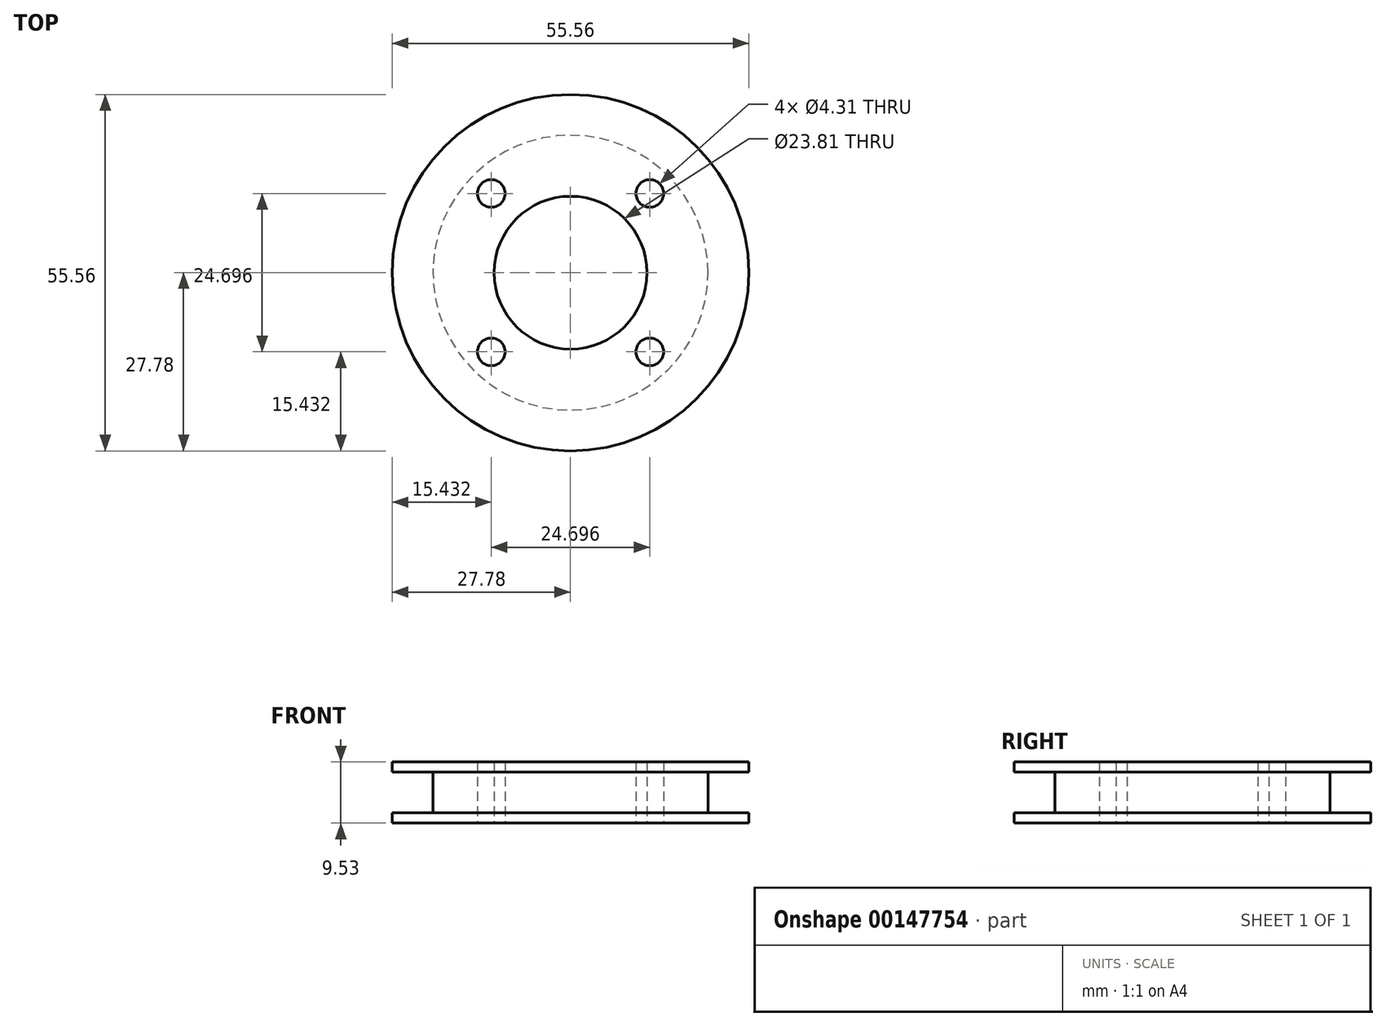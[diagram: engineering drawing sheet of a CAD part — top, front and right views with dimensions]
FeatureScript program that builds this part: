
annotation { "Feature Type Name" : "Feature", "Feature Type Description" : "" }
export const myFeature = defineFeature(function(context is Context, id is Id, definition is map)
    precondition{}
    {
        {
            var Q0;
            Q0=qCreatedBy(makeId("Top.planeOp"),FACE);
            var sketch = newSketch(context, id + "F0", { "sketchPlane" : qUnion([Q0])});
            skCircle(sketch, "E0", {"center": v(0, 0) * mm, "radius": 27.78 * mm});
            skCircle(sketch, "E1", {"center": v(0, 0) * mm, "radius": 11.9 * mm});
            skLineSegment(sketch, "E2.bottom", {"start": v(-12.35, 12.35) * mm, "end": v(12.35, 12.35) * mm, "construction": true});
            skLineSegment(sketch, "E2.top", {"start": v(-12.35, -12.35) * mm, "end": v(12.35, -12.35) * mm, "construction": true});
            skLineSegment(sketch, "E2.left", {"start": v(-12.35, 12.35) * mm, "end": v(-12.35, -12.35) * mm, "construction": true});
            skLineSegment(sketch, "E2.right", {"start": v(12.35, 12.35) * mm, "end": v(12.35, -12.35) * mm, "construction": true});
            skCircle(sketch, "E3", {"center": v(-12.35, 12.35) * mm, "radius": 5.56 * mm, "construction": true});
            skCircle(sketch, "E4", {"center": v(12.35, 12.35) * mm, "radius": 2.15 * mm});
            skCircle(sketch, "E5", {"center": v(-12.35, 12.35) * mm, "radius": 2.15 * mm});
            skCircle(sketch, "E6", {"center": v(-12.35, -12.35) * mm, "radius": 2.15 * mm});
            skCircle(sketch, "E7", {"center": v(12.35, -12.35) * mm, "radius": 2.15 * mm});
            skSolve(sketch);
        }
        {
            var Q0;
            Q0=qSketchRegion(id+"F0",true);
            extrude(context, id + "F1", {"entities" : qUnion([Q0]), "depth" : 9.52 * mm});
        }
        {
            var Q0;
            Q0=qCreatedBy(makeId("Front.planeOp"),FACE);
            var sketch = newSketch(context, id + "F2", { "sketchPlane" : qUnion([Q0])});
            skLineSegment(sketch, "E8.bottom", {"start": v(-42.86, 7.94) * mm, "end": v(-21.43, 7.94) * mm});
            skLineSegment(sketch, "E8.top", {"start": v(-42.86, 1.59) * mm, "end": v(-21.43, 1.59) * mm});
            skLineSegment(sketch, "E8.left", {"start": v(-42.86, 7.94) * mm, "end": v(-42.86, 1.59) * mm});
            skLineSegment(sketch, "E8.right", {"start": v(-21.43, 7.94) * mm, "end": v(-21.43, 1.59) * mm});
            skLineSegment(sketch, "E9", {"start": v(-21.43, 7.94) * mm, "end": v(-21.43, 9.53) * mm, "construction": true});
            skLineSegment(sketch, "E10", {"start": v(-21.43, 9.53) * mm, "end": v(0, 9.53) * mm, "construction": true});
            skLineSegment(sketch, "E11", {"start": v(-21.43, 1.59) * mm, "end": v(-21.43, 0) * mm, "construction": true});
            skLineSegment(sketch, "E12", {"start": v(-21.43, 0) * mm, "end": v(0, 0) * mm, "construction": true});
            skSolve(sketch);
        }
        {
            var Q0;
            Q0=qSketchRegion(id+"F2",true);
            var Q1;
            Q1=makeQuery(id+"F1.opExtrude","SWEPT_FACE",FACE,{"disambiguationData":[OSD([sQuery(id+"F0.wireOp",EDGE,"E0")])]});
            revolve(context, id + "F3", {"operationType" : NewBodyOperationType.REMOVE, "entities" : qUnion([Q0]), "axis" : qUnion([Q1]), "revolveType" : RevolveType.FULL, "oppositeDirection" : true});
        }
    });
